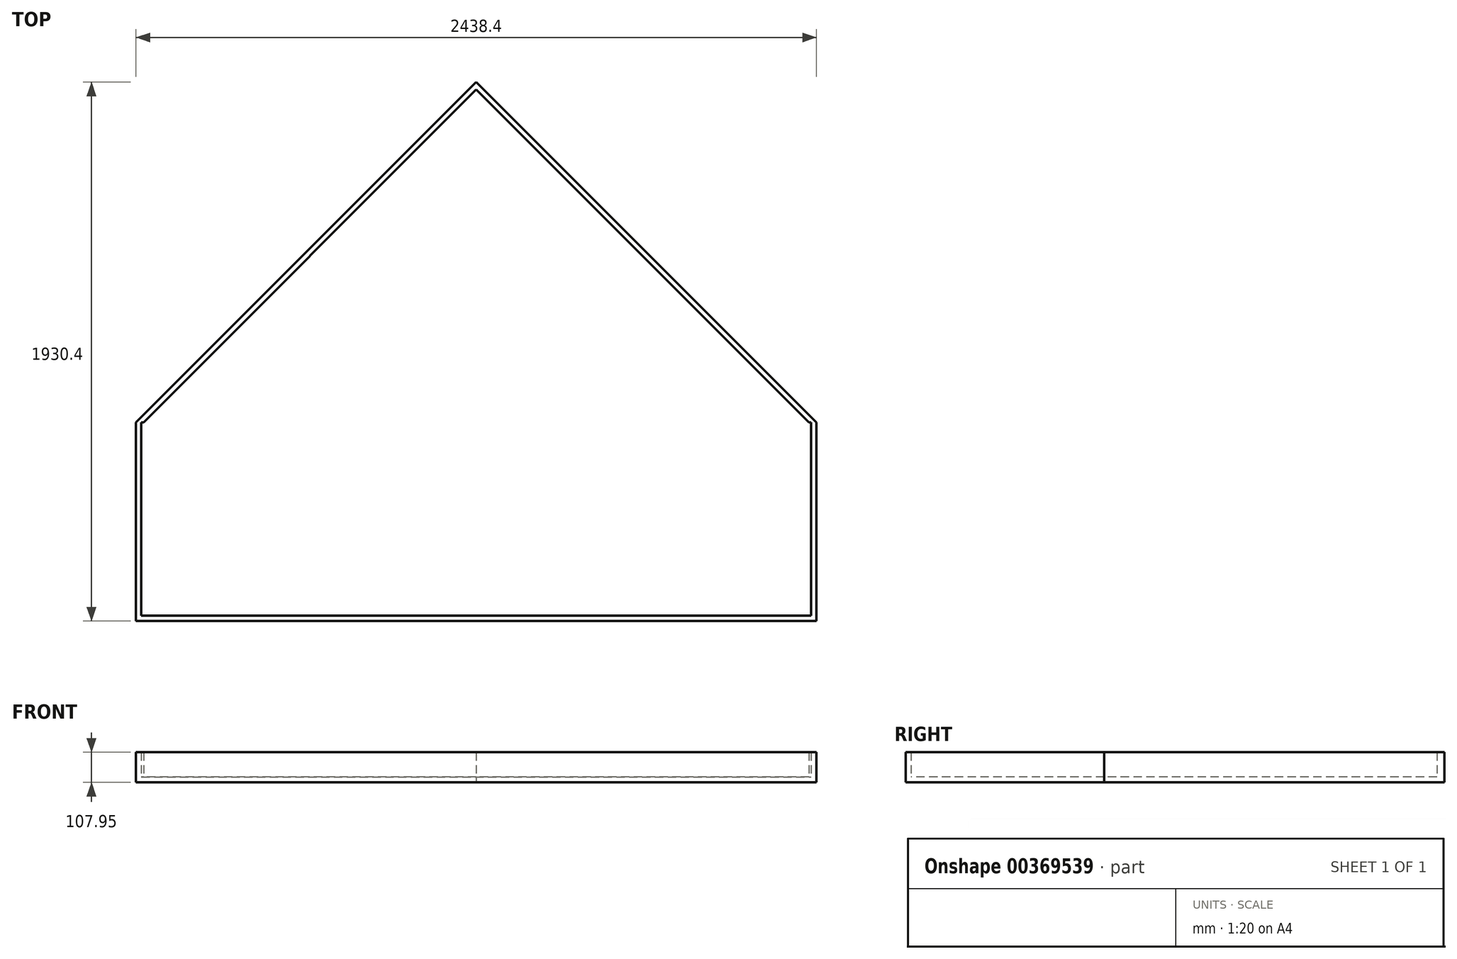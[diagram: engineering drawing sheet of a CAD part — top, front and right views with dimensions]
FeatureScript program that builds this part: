
annotation { "Feature Type Name" : "Feature", "Feature Type Description" : "" }
export const myFeature = defineFeature(function(context is Context, id is Id, definition is map)
    precondition{}
    {
        {
            var Q0;
            Q0=qCreatedBy(makeId("Top.planeOp"),FACE);
            var sketch = newSketch(context, id + "F0", { "sketchPlane" : qUnion([Q0])});
            skLineSegment(sketch, "E0.top", {"start": v(-1219.2, -937.02) * mm, "end": v(1219.2, -937.02) * mm});
            skLineSegment(sketch, "E1", {"start": v(-1219.2, -225.82) * mm, "end": v(-1219.2, -937.02) * mm});
            skLineSegment(sketch, "E2", {"start": v(1219.2, -937.02) * mm, "end": v(1219.2, -225.82) * mm});
            skLineSegment(sketch, "E3", {"start": v(-1219.2, -225.82) * mm, "end": v(0, 993.38) * mm});
            skLineSegment(sketch, "E4", {"start": v(0, 993.38) * mm, "end": v(1219.2, -225.82) * mm});
            skSolve(sketch);
        }
        {
            var Q0;
            Q0 = qSketchRegion(id + "F0", true);
            extrude(context, id + "F1", {"entities" : qUnion([Q0]), "depth" : 19.05 * mm});
        }
        {
            var Q0;
            Q0=makeQuery(id+"F1.opExtrude","CAP_FACE",FACE,{"disambiguationData":[OSD([sQuery(id+"F0.wireOp",EDGE,"E0.top"),sQuery(id+"F0.wireOp",EDGE,"E1"),sQuery(id+"F0.wireOp",EDGE,"E2"),sQuery(id+"F0.wireOp",EDGE,"E3"),sQuery(id+"F0.wireOp",EDGE,"E4")])],"isStart":false});
            var sketch = newSketch(context, id + "F2", { "sketchPlane" : qUnion([Q0])});
            skLineSegment(sketch, "E5.bottom", {"start": v(-1219.2, -937.02) * mm, "end": v(1219.2, -937.02) * mm});
            skLineSegment(sketch, "E5.top", {"start": v(-1219.2, -917.97) * mm, "end": v(1219.2, -917.97) * mm});
            skLineSegment(sketch, "E5.left", {"start": v(-1219.2, -937.02) * mm, "end": v(-1219.2, -917.97) * mm});
            skLineSegment(sketch, "E5.right", {"start": v(1219.2, -937.02) * mm, "end": v(1219.2, -917.97) * mm});
            skLineSegment(sketch, "E6.bottom", {"start": v(-1219.2, -225.82) * mm, "end": v(-1200.15, -225.82) * mm});
            skLineSegment(sketch, "E6.top", {"start": v(-1219.2, -917.97) * mm, "end": v(-1200.15, -917.97) * mm});
            skLineSegment(sketch, "E6.left", {"start": v(-1219.2, -225.82) * mm, "end": v(-1219.2, -917.97) * mm});
            skLineSegment(sketch, "E6.right", {"start": v(-1200.15, -225.82) * mm, "end": v(-1200.15, -917.97) * mm});
            skLineSegment(sketch, "E7.bottom", {"start": v(1219.2, -225.82) * mm, "end": v(1200.15, -225.82) * mm});
            skLineSegment(sketch, "E7.top", {"start": v(1219.2, -917.97) * mm, "end": v(1200.15, -917.97) * mm});
            skLineSegment(sketch, "E7.left", {"start": v(1219.2, -225.82) * mm, "end": v(1219.2, -917.97) * mm});
            skLineSegment(sketch, "E7.right", {"start": v(1200.15, -225.82) * mm, "end": v(1200.15, -917.97) * mm});
            skLineSegment(sketch, "E8", {"start": v(-1219.2, -225.82) * mm, "end": v(0, 993.38) * mm});
            skLineSegment(sketch, "E9", {"start": v(0, 993.38) * mm, "end": v(13.47, 979.9) * mm});
            skLineSegment(sketch, "E10", {"start": v(13.47, 979.9) * mm, "end": v(-1192.26, -225.82) * mm});
            skLineSegment(sketch, "E11", {"start": v(-1192.26, -225.82) * mm, "end": v(-1219.2, -225.82) * mm});
            skLineSegment(sketch, "E12", {"start": v(13.47, 979.9) * mm, "end": v(1219.2, -225.82) * mm});
            skLineSegment(sketch, "E13", {"start": v(1192.26, -225.82) * mm, "end": v(0, 966.44) * mm});
            skLineSegment(sketch, "E14", {"start": v(0, 966.44) * mm, "end": v(13.47, 979.9) * mm});
            skLineSegment(sketch, "E15", {"start": v(1192.26, -225.82) * mm, "end": v(1219.2, -225.82) * mm});
            skLineSegment(sketch, "E16.bottom", {"start": v(-1200.15, -225.82) * mm, "end": v(1200.15, -225.82) * mm});
            skLineSegment(sketch, "E16.top", {"start": v(-1200.15, -244.87) * mm, "end": v(1200.15, -244.87) * mm});
            skLineSegment(sketch, "E16.left", {"start": v(-1200.15, -225.82) * mm, "end": v(-1200.15, -244.87) * mm});
            skLineSegment(sketch, "E16.right", {"start": v(1200.15, -225.82) * mm, "end": v(1200.15, -244.87) * mm});
            skLineSegment(sketch, "E17.bottom", {"start": v(-9.53, -917.97) * mm, "end": v(9.52, -917.97) * mm});
            skLineSegment(sketch, "E17.top", {"start": v(-9.53, -244.87) * mm, "end": v(9.52, -244.87) * mm});
            skLineSegment(sketch, "E17.left", {"start": v(-9.53, -917.97) * mm, "end": v(-9.53, -244.87) * mm});
            skLineSegment(sketch, "E17.right", {"start": v(9.52, -917.97) * mm, "end": v(9.52, -244.87) * mm});
            skLineSegment(sketch, "E18.bottom", {"start": v(-619.13, -244.87) * mm, "end": v(-600.08, -244.87) * mm});
            skLineSegment(sketch, "E18.top", {"start": v(-619.13, -917.97) * mm, "end": v(-600.08, -917.97) * mm});
            skLineSegment(sketch, "E18.left", {"start": v(-619.13, -244.87) * mm, "end": v(-619.13, -917.97) * mm});
            skLineSegment(sketch, "E18.right", {"start": v(-600.08, -244.87) * mm, "end": v(-600.08, -917.97) * mm});
            skLineSegment(sketch, "E19.bottom", {"start": v(600.08, -244.87) * mm, "end": v(619.12, -244.87) * mm});
            skLineSegment(sketch, "E19.top", {"start": v(600.08, -917.97) * mm, "end": v(619.13, -917.97) * mm});
            skLineSegment(sketch, "E19.left", {"start": v(600.08, -244.87) * mm, "end": v(600.08, -917.97) * mm});
            skLineSegment(sketch, "E19.right", {"start": v(619.12, -244.87) * mm, "end": v(619.13, -917.97) * mm});
            skLineSegment(sketch, "E20", {"start": v(-609.6, -244.87) * mm, "end": v(-609.6, -917.97) * mm, "construction": true});
            skLineSegment(sketch, "E21", {"start": v(0, -917.97) * mm, "end": v(0, -244.87) * mm, "construction": true});
            skLineSegment(sketch, "E22", {"start": v(609.6, -244.87) * mm, "end": v(609.6, -917.97) * mm, "construction": true});
            skLineSegment(sketch, "E23", {"start": v(-573.13, 393.3) * mm, "end": v(573.13, 393.3) * mm});
            skLineSegment(sketch, "E24", {"start": v(573.13, 393.3) * mm, "end": v(592.18, 374.25) * mm});
            skLineSegment(sketch, "E25", {"start": v(592.18, 374.25) * mm, "end": v(-592.18, 374.25) * mm});
            skLineSegment(sketch, "E26", {"start": v(-592.18, 374.25) * mm, "end": v(-573.13, 393.3) * mm});
            skLineSegment(sketch, "E27.bottom", {"start": v(-347.7, 374.25) * mm, "end": v(-328.66, 374.25) * mm});
            skLineSegment(sketch, "E27.top", {"start": v(-347.7, -225.82) * mm, "end": v(-328.66, -225.82) * mm});
            skLineSegment(sketch, "E27.left", {"start": v(-347.7, 374.25) * mm, "end": v(-347.7, -225.82) * mm});
            skLineSegment(sketch, "E27.right", {"start": v(-328.66, 374.25) * mm, "end": v(-328.66, -225.82) * mm});
            skLineSegment(sketch, "E28.bottom", {"start": v(347.7, 374.25) * mm, "end": v(328.66, 374.25) * mm});
            skLineSegment(sketch, "E28.top", {"start": v(347.7, -225.82) * mm, "end": v(328.66, -225.82) * mm});
            skLineSegment(sketch, "E28.left", {"start": v(347.7, 374.25) * mm, "end": v(347.7, -225.82) * mm});
            skLineSegment(sketch, "E28.right", {"start": v(328.66, 374.25) * mm, "end": v(328.66, -225.82) * mm});
            skLineSegment(sketch, "E29", {"start": v(-338.18, 374.25) * mm, "end": v(-338.18, -225.82) * mm, "construction": true});
            skLineSegment(sketch, "E30", {"start": v(338.18, -225.82) * mm, "end": v(338.18, 374.25) * mm, "construction": true});
            skLineSegment(sketch, "E31", {"start": v(-582.66, 383.78) * mm, "end": v(582.66, 383.78) * mm, "construction": true});
            skLineSegment(sketch, "E32", {"start": v(-1200.15, -235.35) * mm, "end": v(1200.15, -235.35) * mm, "construction": true});
            skSolve(sketch);
        }
        {
            var Q0;
            Q0 = qSketchRegion(id + "F2", true);
            extrude(context, id + "F3", {"entities" : qUnion([Q0]), "operationType" : NewBodyOperationType.ADD, "depth" : 88.9 * mm});
        }
    });
